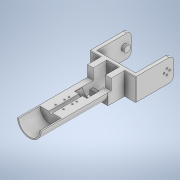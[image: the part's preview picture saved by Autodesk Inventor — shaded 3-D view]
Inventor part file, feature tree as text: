
AUTODESK INVENTOR PART (.ipt)
format: ipt  version: 2022 (Build 260153000, 153)  size: 384,000 bytes
history: native  units: mm
features: extrude x19, sketch x19, fillet x2
ambient origin geometry x8: Origin, YZ Plane, XZ Plane, XY Plane, X Axis, Y Axis, Z Axis, Center Point
bodies: Solid1 (feature_tree)
feature tree (40):
  extrude  "Extrusion1"  Depth=70.0mm
  extrude  "Extrusion2"  Depth=40.0mm TaperAngle=0.0deg
  extrude  "Extrusion3"  Depth=3.0mm
  fillet  "Fillet1"  Radius=40.0mm
  extrude  "Extrusion4"  Depth=4.0mm
  extrude  "Extrusion5"  Depth=5.0mm TaperAngle=0.0deg
  extrude  "Extrusion6"  Depth=11.0mm
  extrude  "Extrusion7"  Depth=5.0mm
  extrude  "Extrusion8"  Depth=24.0mm TaperAngle=0.0deg
  extrude  "Extrusion9"  Depth=6.0mm TaperAngle=0.0deg
  extrude  "Extrusion10"  Depth=33.7mm
  extrude  "Extrusion11"  Depth=13.8mm TaperAngle=0.0deg
  extrude  "Extrusion12"  Depth=50.0mm TaperAngle=0.0deg
  fillet  "Fillet3"  Radius=50.0mm
  extrude  "Extrusion19"  Depth=36.0mm
  extrude  "Extrusion20"  Depth=6.2mm TaperAngle=0.0deg
  extrude  "Extrusion21"  Depth=10.0mm TaperAngle=0.0deg
  extrude  "Extrusion22"  Depth=10.0mm TaperAngle=0.0deg
  extrude  "Extrusion23"  Depth=10.0mm TaperAngle=0.0deg
  extrude  "Extrusion24"  Depth=4.0mm
  extrude  "Extrusion25"  Depth=6.0mm
  sketch  "Sketch1"  dims[d0=62.0mm d1=70.0mm]
  sketch  "Sketch2"  dims[d2=6.0mm d3=40.0mm d4=0.0mm]
  sketch  "Sketch3"  dims[d5=62.0mm d9=3.0mm d10=40.0mm d12=360.0deg]
  sketch  "Sketch4"  dims[d14=40.0mm d15=0.0mm d16=4.0mm]
  sketch  "Sketch5"  dims[d18=11.5mm d19=5.0mm d20=0.0mm]
  sketch  "Sketch6"  dims[d21=8.0mm d22=11.0mm]
  sketch  "Sketch8"  dims[d23=11.0mm d24=5.0mm]
  sketch  "Sketch9"  dims[d25=5.0mm d26=24.0mm d27=0.0mm]
  sketch  "Sketch10"  dims[d29=6.0mm d30=6.0mm d31=0.0mm]
  sketch  "Sketch11"  dims[d32=13.8mm d33=0.0mm d37=33.7mm]
  sketch  "Sketch12"  dims[d38=11.0mm d39=13.8mm d40=0.0mm]
  sketch  "Sketch13"  dims[d41=6.0mm d42=50.0mm d43=0.0mm d44=50.0mm d45=0.0mm]
  sketch  "Sketch20"  dims[d47=36.0mm d48=0.0mm d49=38.0mm]
  sketch  "Sketch21"  dims[d50=32.0mm d51=0.0mm d52=6.2mm d53=0.0mm]
  sketch  "Sketch22"  dims[d63=1.0mm d69=10.0mm d70=0.0mm]
  sketch  "Sketch23"  dims[d71=10.0mm d72=0.0mm d73=10.0mm d74=0.0mm]
  sketch  "Sketch24"  dims[d75=10.0mm d76=0.0mm d77=10.0mm d78=0.0mm]
  sketch  "Sketch25"  dims[d84=0.0mm d85=0.0mm d86=4.0mm]
  sketch  "Sketch26"  dims[d90=2.5mm d91=6.0mm d92=10.0mm d93=0.0mm]
